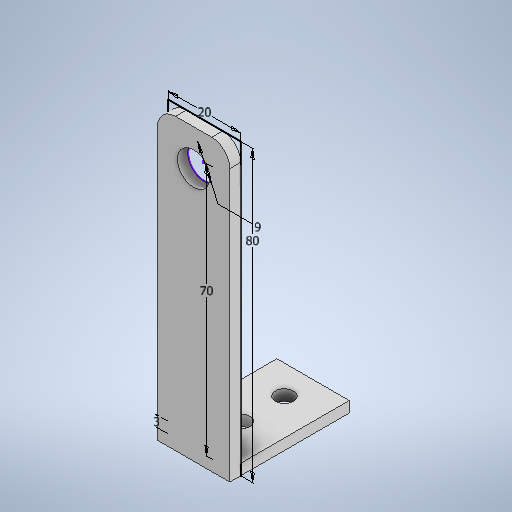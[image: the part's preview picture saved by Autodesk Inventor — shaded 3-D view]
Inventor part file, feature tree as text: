
AUTODESK INVENTOR PART (.ipt)
format: ipt  version: 2025.1 (Build 291241020, 241B)  size: 274,432 bytes
history: native  units: mm
features: extrude x4, sketch x2, fillet x1
ambient origin geometry x8: Origin, YZ Plane, XZ Plane, XY Plane, X Axis, Y Axis, Z Axis, Center Point
bodies: Solid1 (feature_tree)
feature tree (7):
  sketch  "Sketch1"  dims[d0=20.0mm d1=80.0mm d2=9.0mm]
  extrude  "Extrusion1"  Depth=80.0mm
  fillet  "Fillet1"  Radius=9.0mm
  extrude  "Extrusion2"  Depth=3.0mm TaperAngle=0.0deg
  extrude  "Extrusion3"  Depth=5.0mm
  extrude  "Extrusion4"  Depth=3.0mm
  sketch  "Sketch2"  dims[d3=70.0mm d4=3.0mm d5=0.0mm d6=5.0mm d7=3.0mm d8=30.0mm d9=0.0mm d10=5.0mm d11=5.0mm d12=0.0mm d13=0.0mm d14=10.0mm d15=0.0mm d16=0.5mm d17=0.872665mm]
